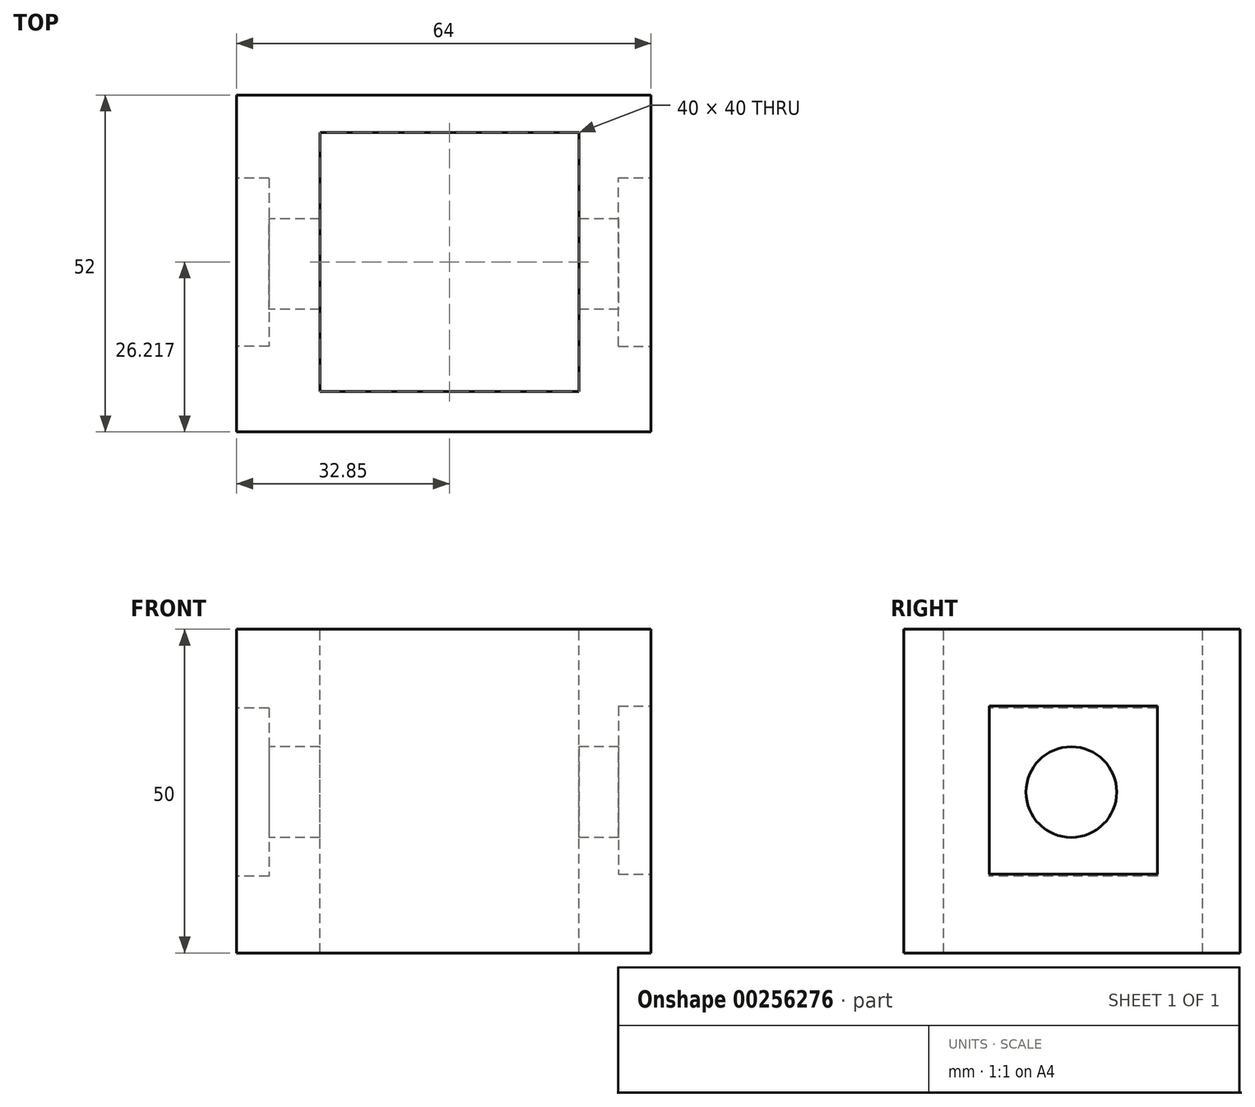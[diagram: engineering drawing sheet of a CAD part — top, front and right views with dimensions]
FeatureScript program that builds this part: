
annotation { "Feature Type Name" : "Feature", "Feature Type Description" : "" }
export const myFeature = defineFeature(function(context is Context, id is Id, definition is map)
    precondition{}
    {
        {
            var Q0;
            Q0=qCreatedBy(makeId("Top.planeOp"),FACE);
            var sketch = newSketch(context, id + "F0", { "sketchPlane" : qUnion([Q0])});
            skLineSegment(sketch, "E0.bottom", {"start": v(-52.85, -32.27) * mm, "end": v(11.15, -32.27) * mm});
            skLineSegment(sketch, "E0.top", {"start": v(-52.85, 19.73) * mm, "end": v(11.15, 19.73) * mm});
            skLineSegment(sketch, "E0.left", {"start": v(-52.85, -32.27) * mm, "end": v(-52.85, 19.73) * mm});
            skLineSegment(sketch, "E0.right", {"start": v(11.15, -32.27) * mm, "end": v(11.15, 19.73) * mm});
            skSolve(sketch);
        }
        {
            var Q0;
            Q0=makeQuery(id+"F0.imprint","IMPRINT",FACE,{"disambiguationData":[TD([[makeQuery(id+"F0.imprint","IMPRINT",EDGE,{"derivedFrom":sQuery(id+"F0.wireOp",EDGE,"E0.bottom")}),1.0]])]});
            extrude(context, id + "F1", {"entities" : qUnion([Q0]), "depth" : 50 * mm});
        }
        {
            var Q0;
            Q0=makeQuery(id+"F1.opExtrude","CAP_FACE",FACE,{"disambiguationData":[OSD([sQuery(id+"F0.wireOp",EDGE,"E0.bottom"),sQuery(id+"F0.wireOp",EDGE,"E0.top"),sQuery(id+"F0.wireOp",EDGE,"E0.left"),sQuery(id+"F0.wireOp",EDGE,"E0.right")])],"isStart":false});
            var sketch = newSketch(context, id + "F2", { "sketchPlane" : qUnion([Q0])});
            skLineSegment(sketch, "E1", {"start": v(11.15, 19.73) * mm, "end": v(11.15, 13.73) * mm});
            skLineSegment(sketch, "E2", {"start": v(11.15, 13.73) * mm, "end": v(11.15, -26.27) * mm});
            skLineSegment(sketch, "E3", {"start": v(11.15, -26.27) * mm, "end": v(11.15, -32.27) * mm});
            skLineSegment(sketch, "E4", {"start": v(11.15, -26.27) * mm, "end": v(-0.85, -26.27) * mm});
            skLineSegment(sketch, "E5", {"start": v(-0.85, -26.27) * mm, "end": v(-40.85, -26.27) * mm});
            skLineSegment(sketch, "E6", {"start": v(-40.85, -26.27) * mm, "end": v(-52.85, -26.27) * mm});
            skSolve(sketch);
        }
        {
            var Q0;
            Q0=makeQuery(id+"F2.imprint","IMPRINT",FACE,{"disambiguationData":[TD([[makeQuery(id+"F2.imprint","IMPRINT",EDGE,{"derivedFrom":sQuery(id+"F2.wireOp",EDGE,"E1")}),1.0]])]});
            var sketch = newSketch(context, id + "F3", { "sketchPlane" : qUnion([Q0])});
            skLineSegment(sketch, "E7.bottom", {"start": v(-40, -26.05) * mm, "end": v(0, -26.05) * mm});
            skLineSegment(sketch, "E7.top", {"start": v(-40, 13.95) * mm, "end": v(0, 13.95) * mm});
            skLineSegment(sketch, "E7.left", {"start": v(-40, -26.05) * mm, "end": v(-40, 13.95) * mm});
            skLineSegment(sketch, "E7.right", {"start": v(0, -26.05) * mm, "end": v(0, 13.95) * mm});
            skSolve(sketch);
        }
        {
            var Q0;
            Q0=makeQuery(id+"F3.imprint","IMPRINT",FACE,{"disambiguationData":[TD([[makeQuery(id+"F3.imprint","IMPRINT",EDGE,{"derivedFrom":sQuery(id+"F3.wireOp",EDGE,"E7.bottom")}),1.0]])]});
            extrude(context, id + "F4", {"entities" : qUnion([Q0]), "operationType" : NewBodyOperationType.REMOVE, "oppositeDirection" : true, "depth" : 50 * mm});
        }
        {
            var Q0;
            Q0=makeQuery(id+"F1.opExtrude","SWEPT_FACE",FACE,{"disambiguationData":[OSD([sQuery(id+"F0.wireOp",EDGE,"E0.right")])]});
            var sketch = newSketch(context, id + "F5", { "sketchPlane" : qUnion([Q0])});
            skLineSegment(sketch, "E8.bottom", {"start": v(-19.04, 38.14) * mm, "end": v(6.96, 38.14) * mm});
            skLineSegment(sketch, "E8.top", {"start": v(-19.04, 12.14) * mm, "end": v(6.96, 12.14) * mm});
            skLineSegment(sketch, "E8.left", {"start": v(-19.04, 38.14) * mm, "end": v(-19.04, 12.14) * mm});
            skLineSegment(sketch, "E8.right", {"start": v(6.96, 38.14) * mm, "end": v(6.96, 12.14) * mm});
            skSolve(sketch);
        }
        {
            var Q0;
            Q0=makeQuery(id+"F5.imprint","IMPRINT",FACE,{"disambiguationData":[TD([[makeQuery(id+"F5.imprint","IMPRINT",EDGE,{"derivedFrom":sQuery(id+"F5.wireOp",EDGE,"E8.bottom")}),-1.0]])]});
            extrude(context, id + "F6", {"entities" : qUnion([Q0]), "operationType" : NewBodyOperationType.REMOVE, "oppositeDirection" : true, "depth" : 5 * mm});
        }
        {
            var Q0;
            Q0=makeQuery(id+"F1.opExtrude","SWEPT_FACE",FACE,{"disambiguationData":[OSD([sQuery(id+"F0.wireOp",EDGE,"E0.left")])]});
            var sketch = newSketch(context, id + "F7", { "sketchPlane" : qUnion([Q0])});
            skLineSegment(sketch, "E9.bottom", {"start": v(-6.9, 37.84) * mm, "end": v(19.1, 37.84) * mm});
            skLineSegment(sketch, "E9.top", {"start": v(-6.9, 11.84) * mm, "end": v(19.1, 11.84) * mm});
            skLineSegment(sketch, "E9.left", {"start": v(-6.9, 37.84) * mm, "end": v(-6.9, 11.84) * mm});
            skLineSegment(sketch, "E9.right", {"start": v(19.1, 37.84) * mm, "end": v(19.1, 11.84) * mm});
            skSolve(sketch);
        }
        {
            var Q0;
            Q0=makeQuery(id+"F7.imprint","IMPRINT",FACE,{"disambiguationData":[TD([[makeQuery(id+"F7.imprint","IMPRINT",EDGE,{"derivedFrom":sQuery(id+"F7.wireOp",EDGE,"E9.bottom")}),-1.0]])]});
            extrude(context, id + "F8", {"entities" : qUnion([Q0]), "operationType" : NewBodyOperationType.REMOVE, "oppositeDirection" : true, "depth" : 5 * mm});
        }
        {
            var Q0;
            Q0=makeQuery(id+"F8.boolean.opBoolean","COPY",FACE,{"derivedFrom":makeQuery(id+"F8.opExtrude","CAP_FACE",FACE,{"disambiguationData":[OSD([sQuery(id+"F7.wireOp",EDGE,"E9.bottom"),sQuery(id+"F7.wireOp",EDGE,"E9.top"),sQuery(id+"F7.wireOp",EDGE,"E9.left"),sQuery(id+"F7.wireOp",EDGE,"E9.right")])],"isStart":false})});
            var sketch = newSketch(context, id + "F9", { "sketchPlane" : qUnion([Q0])});
            skCircle(sketch, "E10", {"center": v(6.37, 24.84) * mm, "radius": 7 * mm});
            skPoint(sketch, "E10.centerSnap0", {"position": v(-6.9, 24.84) * mm});
            skSolve(sketch);
        }
        {
            var Q0;
            Q0=makeQuery(id+"F9.imprint","IMPRINT",FACE,{"disambiguationData":[TD([[makeQuery(id+"F9.imprint","IMPRINT",EDGE,{"derivedFrom":sQuery(id+"F9.wireOp",EDGE,"E10")}),1.0]])]});
            extrude(context, id + "F10", {"entities" : qUnion([Q0]), "operationType" : NewBodyOperationType.REMOVE, "oppositeDirection" : true, "depth" : 64 * mm});
        }
    });
